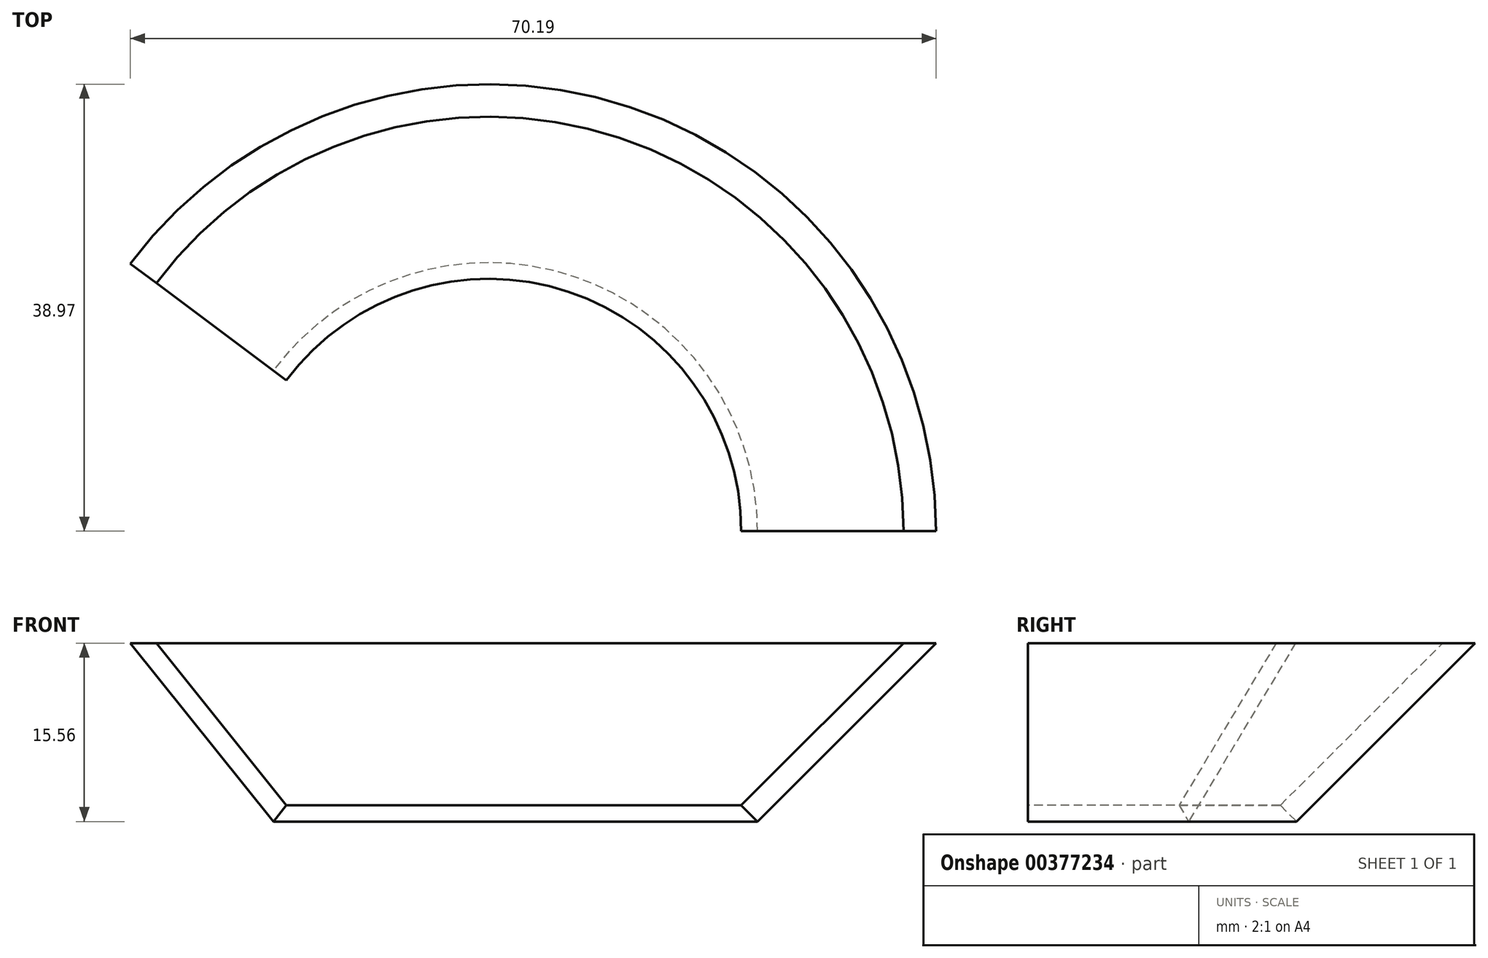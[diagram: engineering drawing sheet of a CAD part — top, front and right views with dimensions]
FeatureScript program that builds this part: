
annotation { "Feature Type Name" : "Feature", "Feature Type Description" : "" }
export const myFeature = defineFeature(function(context is Context, id is Id, definition is map)
    precondition{}
    {
        {
            var Q0;
            Q0=qCreatedBy(makeId("Front.planeOp"),FACE);
            var sketch = newSketch(context, id + "F0", { "sketchPlane" : qUnion([Q0])});
            skLineSegment(sketch, "E0", {"start": v(38.97, 15.56) * mm, "end": v(37.56, 16.97) * mm});
            skLineSegment(sketch, "E1", {"start": v(0, 22) * mm, "end": v(0, 0) * mm, "construction": true});
            skLineSegment(sketch, "E2", {"start": v(37.56, 16.97) * mm, "end": v(22, 1.41) * mm});
            skLineSegment(sketch, "E3", {"start": v(38.97, 15.56) * mm, "end": v(23.41, 0) * mm});
            skLineSegment(sketch, "E4", {"start": v(22, 1.41) * mm, "end": v(23.41, 0) * mm});
            skSolve(sketch);
        }
        {
            var Q0;
            Q0=makeQuery(id+"F0.imprint","IMPRINT",FACE,{"disambiguationData":[TD([[makeQuery(id+"F0.imprint","IMPRINT",EDGE,{"derivedFrom":sQuery(id+"F0.wireOp",EDGE,"3R4KFfJ1-Y3Kb-D4CS-npq4-7DWoadC4dx8a")}),1.0]])]});
            var Q1;
            Q1=makeQuery(id+"F0.imprint","IMPRINT",FACE,{"disambiguationData":[TD([[makeQuery(id+"F0.imprint","IMPRINT",EDGE,{"derivedFrom":sQuery(id+"F0.wireOp",EDGE,"E0")}),1.0]])]});
            var Q2;
            Q2=sQuery(id+"F0.wireOp",EDGE,"E1");
            revolve(context, id + "F1", {"entities" : qUnion([Q0, Q1]), "axis" : qUnion([Q2]), "revolveType" : RevolveType.ONE_DIRECTION, "oppositeDirection" : true, "angle" : 143.24 * degree, "surfaceOperationType" : NewSurfaceOperationType.NEW});
        }
        {
            var Q0;
            Q0=makeQuery(id+"F1.opRevolve","SWEPT_EDGE",EDGE,{"disambiguationData":[OSD([sQuery(id+"F0.wireOp",EDGE,"E0"),sQuery(id+"F0.wireOp",EDGE,"E2")])]});
            chamfer(context, id + "F2", {"entities" : qUnion([Q0]), "chamferType" : ChamferType.OFFSET_ANGLE, "width" : 2 * mm, "oppositeDirection" : false, "angle" : 45 * degree});
        }
    });
